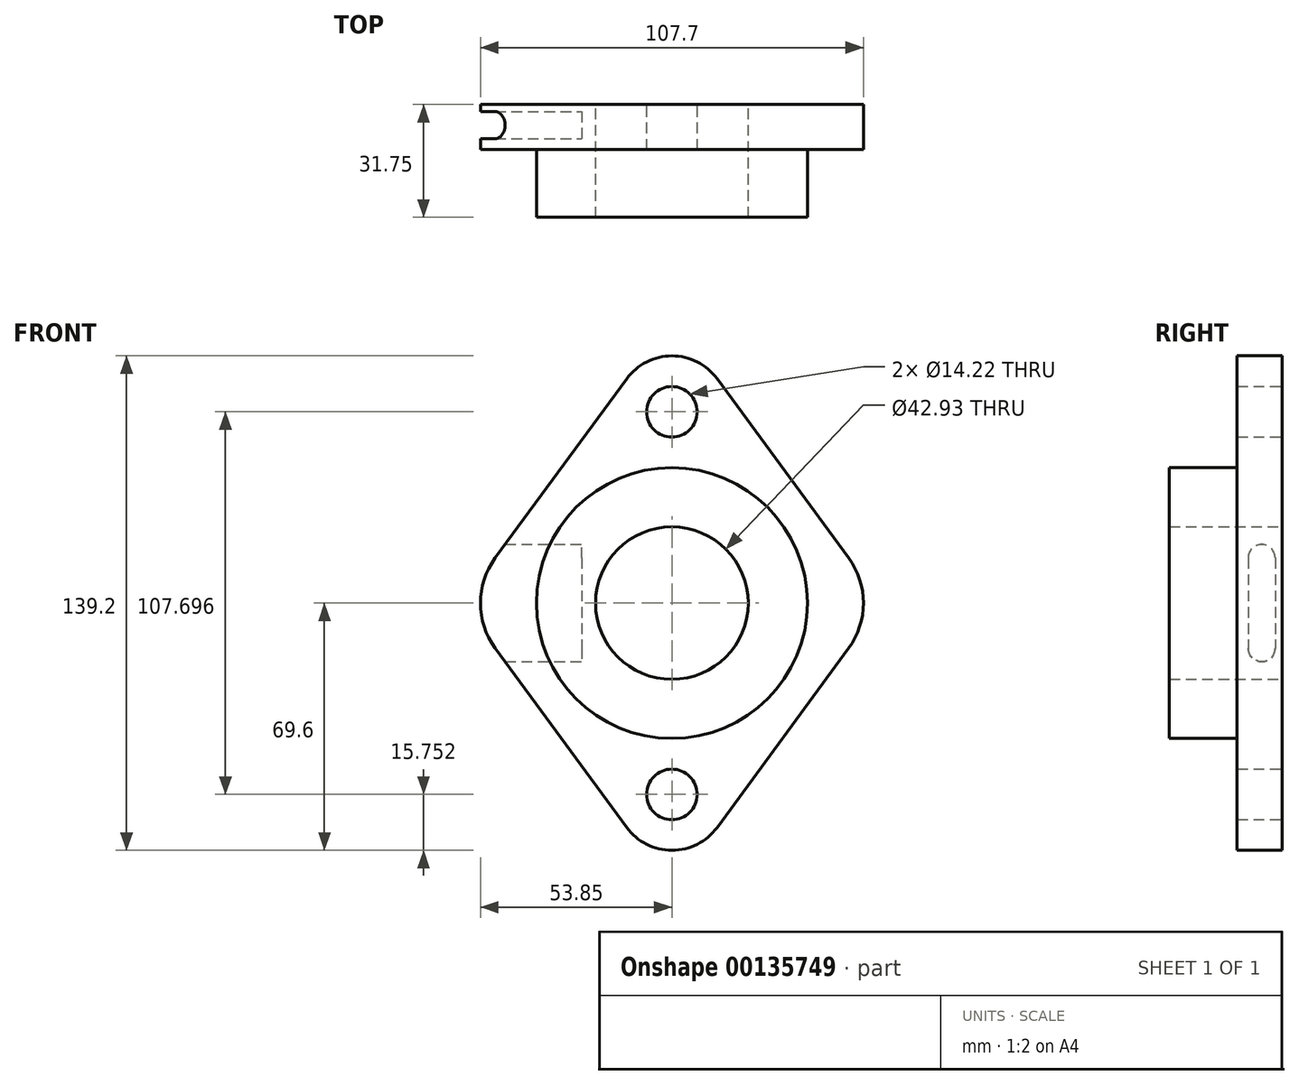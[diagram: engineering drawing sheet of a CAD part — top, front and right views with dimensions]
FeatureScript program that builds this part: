
annotation { "Feature Type Name" : "Feature", "Feature Type Description" : "" }
export const myFeature = defineFeature(function(context is Context, id is Id, definition is map)
    precondition{}
    {
        {
            var Q0;
            Q0=qCreatedBy(makeId("Front.planeOp"),FACE);
            var sketch = newSketch(context, id + "F0", { "sketchPlane" : qUnion([Q0])});
            skCircle(sketch, "E0", {"center": v(0, 0) * mm, "radius": 21.46 * mm});
            skCircle(sketch, "E1", {"center": v(0, 53.85) * mm, "radius": 7.11 * mm});
            skCircle(sketch, "E2", {"center": v(0, -53.85) * mm, "radius": 7.11 * mm});
            skLineSegment(sketch, "E3", {"start": v(0, 53.85) * mm, "end": v(0, -53.85) * mm, "construction": true});
            skArc(sketch, "E4.0.startCap", {"start": v(-12.7, 63.16) * mm, "mid": v(0, 69.6) * mm, "end": v(12.7, 63.16) * mm});
            skArc(sketch, "E4.0.endCap", {"start": v(12.7, -63.16) * mm, "mid": v(0, -69.6) * mm, "end": v(-12.7, -63.16) * mm});
            skLineSegment(sketch, "E5", {"start": v(-12.7, -63.16) * mm, "end": v(-49.7, -12.7) * mm});
            skLineSegment(sketch, "E6", {"start": v(-12.7, 63.16) * mm, "end": v(-49.7, 12.7) * mm});
            skArc(sketch, "E7", {"start": v(-49.7, 12.7) * mm, "mid": v(-53.85, 0) * mm, "end": v(-49.7, -12.7) * mm});
            skLineSegment(sketch, "E8", {"start": v(12.7, -63.16) * mm, "end": v(49.7, -12.7) * mm});
            skLineSegment(sketch, "E9", {"start": v(12.7, 63.16) * mm, "end": v(49.7, 12.7) * mm});
            skArc(sketch, "E10", {"start": v(49.7, 12.7) * mm, "mid": v(53.85, 0) * mm, "end": v(49.7, -12.7) * mm});
            skCircle(sketch, "E11", {"center": v(0, 0) * mm, "radius": 38.1 * mm});
            skSolve(sketch);
        }
        {
            var Q0;
            Q0=makeQuery(id+"F0.imprint","IMPRINT",FACE,{"disambiguationData":[TD([[makeQuery(id+"F0.imprint","IMPRINT",EDGE,{"derivedFrom":sQuery(id+"F0.wireOp",EDGE,"E1")}),-1.0]])]});
            extrude(context, id + "F1", {"entities" : qUnion([Q0]), "depth" : 12.7 * mm});
        }
        {
            var Q0;
            Q0=makeQuery(id+"F0.imprint","IMPRINT",FACE,{"disambiguationData":[TD([[makeQuery(id+"F0.imprint","IMPRINT",EDGE,{"derivedFrom":sQuery(id+"F0.wireOp",EDGE,"E0")}),-1.0]])]});
            extrude(context, id + "F2", {"entities" : qUnion([Q0]), "operationType" : NewBodyOperationType.ADD, "depth" : 31.75 * mm});
        }
        {
            var Q0;
            Q0=qCreatedBy(makeId("Right.planeOp"),FACE);
            var sketch = newSketch(context, id + "F3", { "sketchPlane" : qUnion([Q0])});
            skLineSegment(sketch, "E12", {"start": v(-5.82, 12.7) * mm, "end": v(-5.82, -12.7) * mm, "construction": true});
            skLineSegment(sketch, "E13", {"start": v(-2, 12.7) * mm, "end": v(-2, -12.7) * mm});
            skLineSegment(sketch, "E14", {"start": v(-9.63, 12.7) * mm, "end": v(-9.63, -12.7) * mm});
            skArc(sketch, "E15", {"start": v(-2, 12.7) * mm, "mid": v(-5.82, 16.5) * mm, "end": v(-9.63, 12.7) * mm});
            skArc(sketch, "E16", {"start": v(-2, -12.7) * mm, "mid": v(-5.82, -16.51) * mm, "end": v(-9.63, -12.7) * mm});
            skSolve(sketch);
        }
        {
            var Q0;
            Q0 = qSketchRegion(id + "F3", true);
            extrude(context, id + "F4", {"entities" : qUnion([Q0]), "operationType" : NewBodyOperationType.REMOVE, "oppositeDirection" : true, "depth" : 57.15 * mm, "hasSecondDirection" : true, "secondDirectionOppositeDirection" : true, "secondDirectionDepth" : 25.4 * mm});
        }
    });
